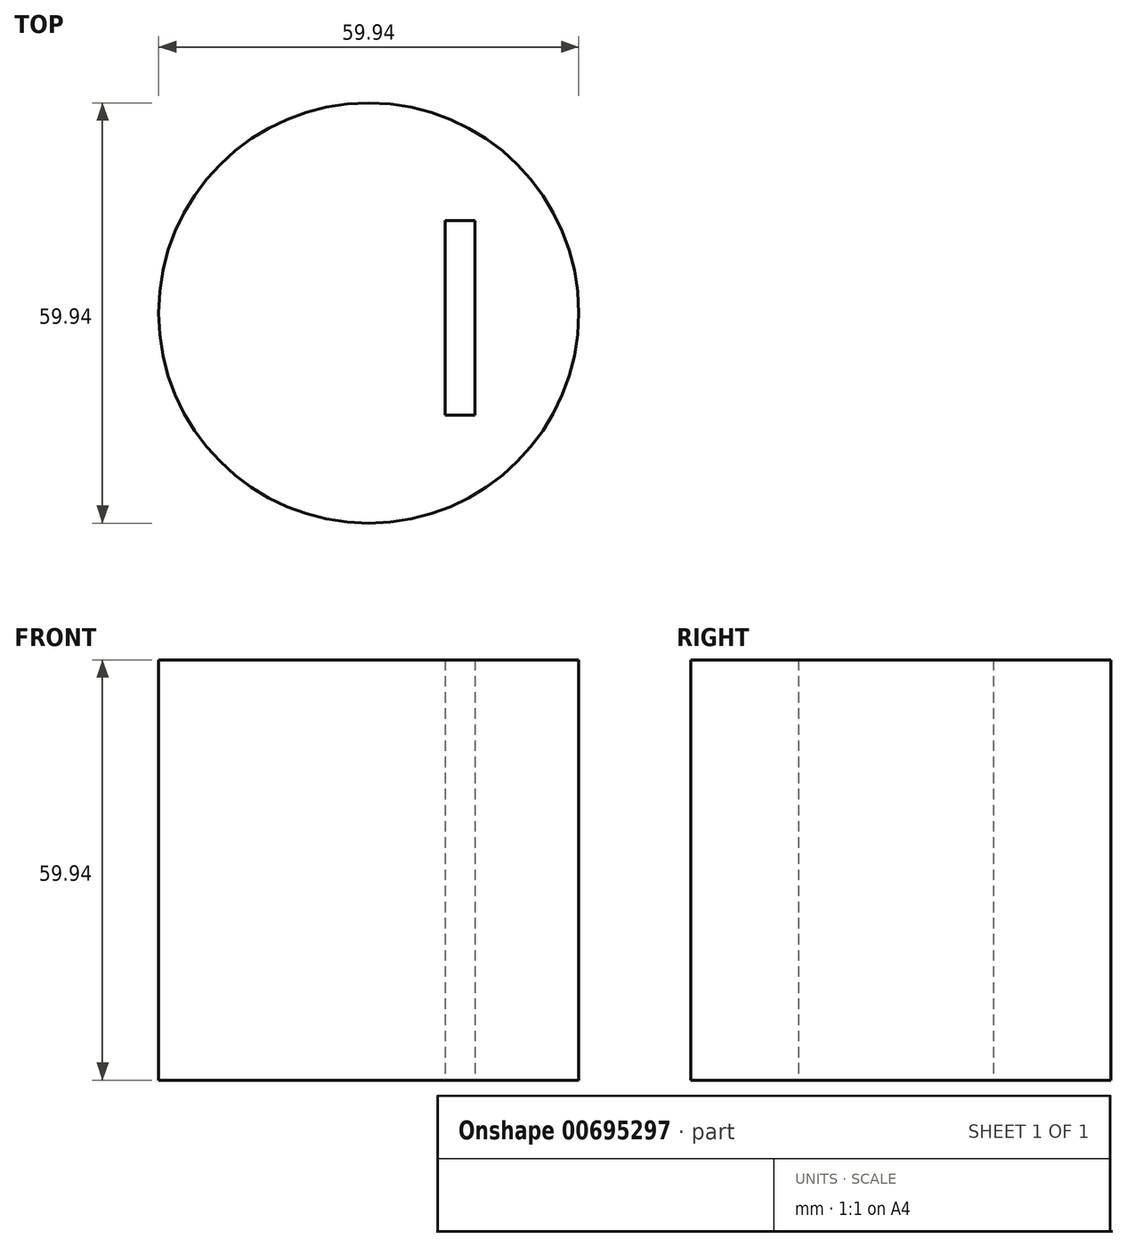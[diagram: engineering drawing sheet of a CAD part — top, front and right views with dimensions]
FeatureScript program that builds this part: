
annotation { "Feature Type Name" : "Feature", "Feature Type Description" : "" }
export const myFeature = defineFeature(function(context is Context, id is Id, definition is map)
    precondition{}
    {
        {
            var Q0;
            Q0=qCreatedBy(makeId("Top.planeOp"),FACE);
            var sketch = newSketch(context, id + "F0", { "sketchPlane" : qUnion([Q0])});
            skCircle(sketch, "E0", {"center": v(0, 0) * mm, "radius": 29.97 * mm});
            skLineSegment(sketch, "E1.bottom", {"start": v(-14.5, 13.18) * mm, "end": v(15.16, 13.18) * mm});
            skLineSegment(sketch, "E1.top", {"start": v(-14.5, -14.6) * mm, "end": v(15.16, -14.6) * mm});
            skLineSegment(sketch, "E1.left", {"start": v(-14.5, 13.18) * mm, "end": v(-14.5, -14.6) * mm});
            skLineSegment(sketch, "E1.right", {"start": v(15.16, 13.18) * mm, "end": v(15.16, -14.6) * mm});
            skSolve(sketch);
        }
        {
            var Q0;
            Q0=makeQuery(id+"F0.imprint","IMPRINT",FACE,{"disambiguationData":[TD([[makeQuery(id+"F0.imprint","IMPRINT",EDGE,{"derivedFrom":sQuery(id+"F0.wireOp",EDGE,"E0")}),1.0]])]});
            extrude(context, id + "F1", {"entities" : qUnion([Q0]), "depth" : 59.94 * mm, "offsetDistance" : 25.4 * mm});
        }
        {
            var Q0;
            Q0=makeQuery(id+"F1.opExtrude","SWEPT_FACE",FACE,{"disambiguationData":[OSD([sQuery(id+"F0.wireOp",EDGE,"E1.left")])]});
            extrude(context, id + "F2", {"entities" : qUnion([Q0]), "operationType" : NewBodyOperationType.ADD, "depth" : 25.4 * mm, "offsetDistance" : 25.4 * mm});
        }
    });
